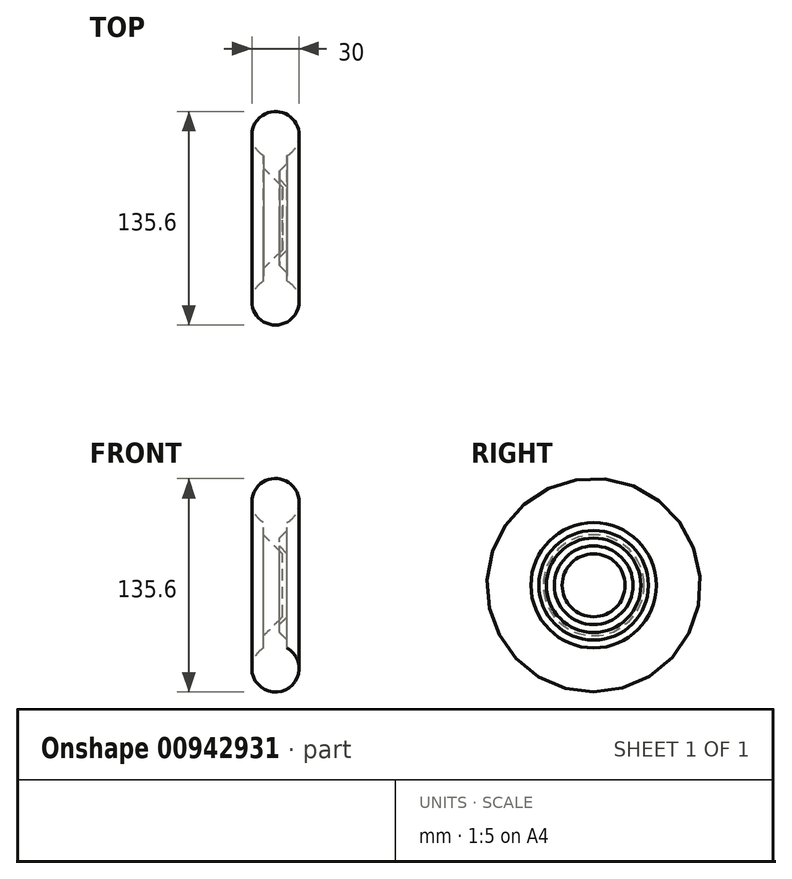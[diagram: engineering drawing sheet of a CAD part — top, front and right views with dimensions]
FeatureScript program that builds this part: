
annotation { "Feature Type Name" : "Feature", "Feature Type Description" : "" }
export const myFeature = defineFeature(function(context is Context, id is Id, definition is map)
    precondition{}
    {
        {
            var Q0;
            Q0=qCreatedBy(makeId("Front.planeOp"),FACE);
            var sketch = newSketch(context, id + "F0", { "sketchPlane" : qUnion([Q0])});
            skArc(sketch, "E0", {"start": v(-28.41, 19.81) * mm, "mid": v(-35.91, 47.8) * mm, "end": v(-43.41, 19.81) * mm});
            skLineSegment(sketch, "E1", {"start": v(-28.41, 19.81) * mm, "end": v(-28.41, 14.81) * mm});
            skLineSegment(sketch, "E2", {"start": v(-33.41, 10) * mm, "end": v(-28.41, 14.81) * mm});
            skLineSegment(sketch, "E3", {"start": v(-33.41, 10) * mm, "end": v(-33.41, 5) * mm});
            skPoint(sketch, "E4.end.orphan", {"position": v(-26.27, 0) * mm});
            skLineSegment(sketch, "E5", {"start": v(-33.41, 5) * mm, "end": v(-28.41, 0) * mm});
            skPoint(sketch, "E6.orphan", {"position": v(-26.27, -38.05) * mm});
            skPoint(sketch, "E7.end.orphan", {"position": v(-37, -38.05) * mm});
            skLineSegment(sketch, "E8", {"start": v(-28.41, 0) * mm, "end": v(-28.41, -20) * mm});
            skLineSegment(sketch, "E9", {"start": v(-61.22, -38.05) * mm, "end": v(-62.94, -38.85) * mm});
            skLineSegment(sketch, "E10", {"start": v(-66.63, -25.87) * mm, "end": v(-67.05, -27.37) * mm});
            skPoint(sketch, "E11.start.orphan", {"position": v(-66.63, -34.7) * mm});
            skPoint(sketch, "E12.end.orphan", {"position": v(-61.22, -34.7) * mm});
            skPoint(sketch, "E13.start.orphan", {"position": v(-37, -25.87) * mm});
            skPoint(sketch, "E14.start.orphan", {"position": v(-47.29, -25.87) * mm});
            skLineSegment(sketch, "E15", {"start": v(-31.41, 0) * mm, "end": v(-31.41, -1.87) * mm});
            skLineSegment(sketch, "E16", {"start": v(-31.41, 0) * mm, "end": v(-43.41, 12) * mm});
            skPoint(sketch, "E17.end.orphan", {"position": v(-52.58, -10.52) * mm});
            skPoint(sketch, "E18.start.orphan", {"position": v(-52.58, -29.68) * mm});
            skLineSegment(sketch, "E19", {"start": v(-28.41, -20) * mm, "end": v(-31.41, -20) * mm});
            skLineSegment(sketch, "E20", {"start": v(-31.41, -20) * mm, "end": v(-31.41, -1.87) * mm});
            skPoint(sketch, "E21.end.orphan", {"position": v(-53, -1.87) * mm});
            skPoint(sketch, "E22.start.orphan", {"position": v(-43.41, 14.81) * mm});
            skLineSegment(sketch, "E23", {"start": v(-43.41, 19.81) * mm, "end": v(-43.41, 12) * mm});
            skPoint(sketch, "E24.start.orphan", {"position": v(-28.41, 32.8) * mm});
            skSolve(sketch);
        }
        {
            var Q0;
            Q0=makeQuery(id+"F0.imprint","IMPRINT",FACE,{"disambiguationData":[TD([[makeQuery(id+"F0.imprint","IMPRINT",EDGE,{"derivedFrom":sQuery(id+"F0.wireOp",EDGE,"ig5zt77j-EQ4V-wuMH-9RIN-2pZxivVrfX0F")}),-1.0]])]});
            var Q1;
            Q1=makeQuery(id+"F0.imprint","IMPRINT",FACE,{"disambiguationData":[TD([[makeQuery(id+"F0.imprint","IMPRINT",EDGE,{"derivedFrom":sQuery(id+"F0.wireOp",EDGE,"ig5zt77j-EQ4V-wuMH-9RIN-2pZxivVrfX0F")}),1.0]])]});
            var Q2;
            Q2=makeQuery(id+"F0.imprint","IMPRINT",FACE,{"disambiguationData":[TD([[makeQuery(id+"F0.imprint","IMPRINT",EDGE,{"derivedFrom":sQuery(id+"F0.wireOp",EDGE,"P19UumjC-ikMn-kLLg-niX1-3UejyW5Ps7u9")}),1.0]])]});
            var Q3;
            Q3=makeQuery(id+"F0.imprint","IMPRINT",FACE,{"disambiguationData":[TD([[makeQuery(id+"F0.imprint","IMPRINT",EDGE,{"derivedFrom":sQuery(id+"F0.wireOp",EDGE,"E8")}),-1.0]])]});
            var Q4;
            Q4=sQuery(id+"F0.wireOp",EDGE,"E19");
            revolve(context, id + "F1", {"surfaceOperationType" : NewSurfaceOperationType.NEW, "entities" : qUnion([Q0, Q1, Q2, Q3]), "axis" : qUnion([Q4]), "revolveType" : RevolveType.FULL});
        }
    });
